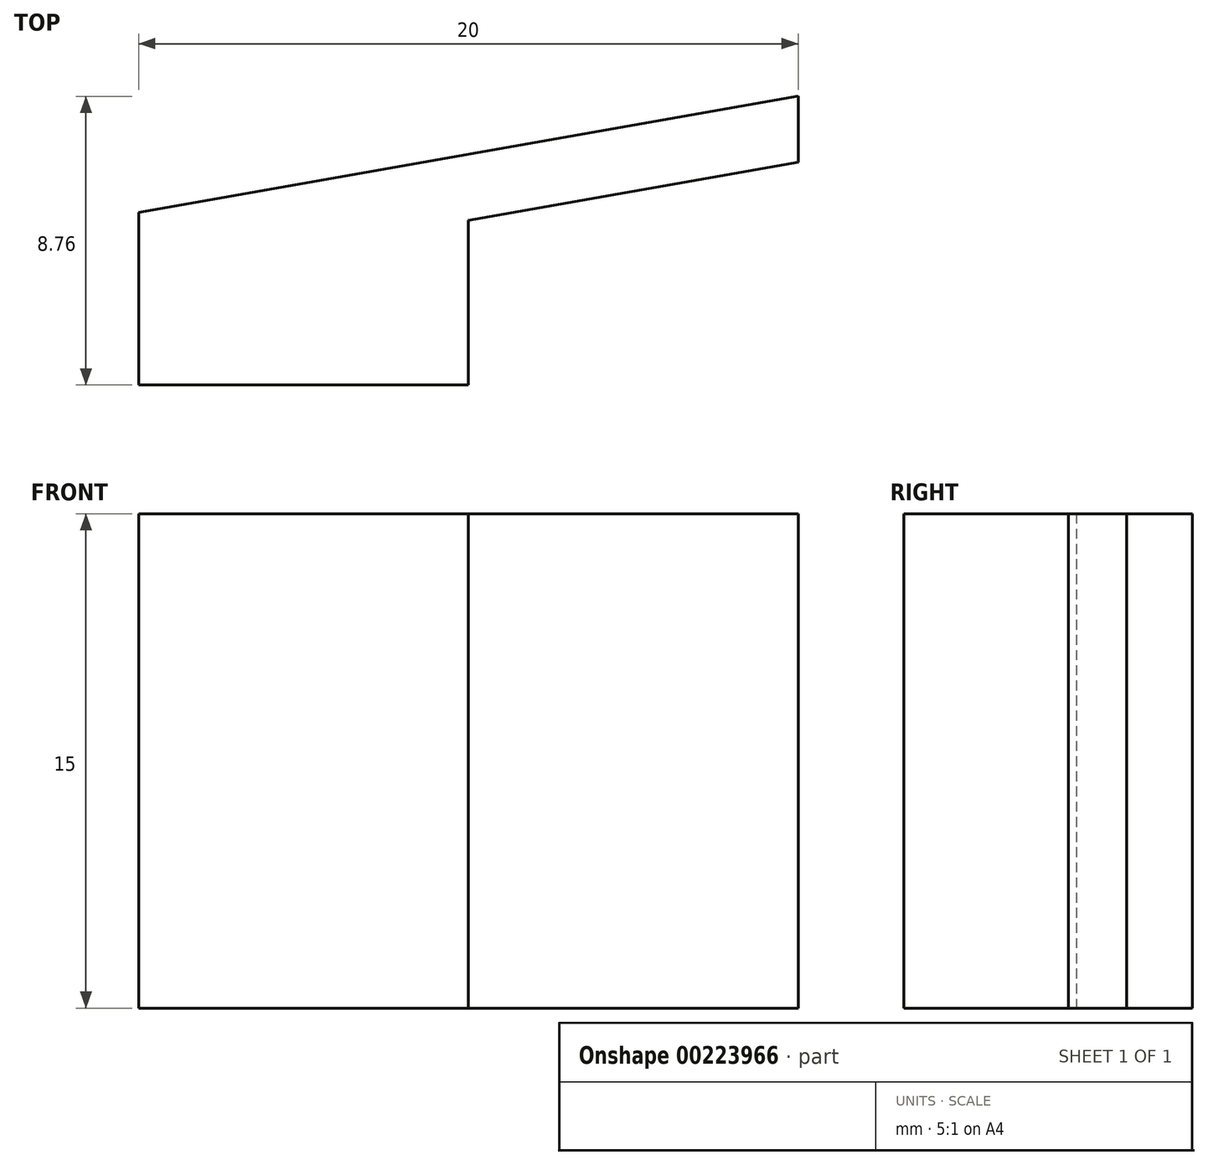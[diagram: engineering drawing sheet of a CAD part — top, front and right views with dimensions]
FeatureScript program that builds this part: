
annotation { "Feature Type Name" : "Feature", "Feature Type Description" : "" }
export const myFeature = defineFeature(function(context is Context, id is Id, definition is map)
    precondition{}
    {
        {
            var Q0;
            Q0=qCreatedBy(makeId("Top.planeOp"),FACE);
            var sketch = newSketch(context, id + "F0", { "sketchPlane" : qUnion([Q0])});
            skLineSegment(sketch, "E0", {"start": v(0, 0) * mm, "end": v(10, 0) * mm});
            skLineSegment(sketch, "E1", {"start": v(10, 0) * mm, "end": v(10, 5) * mm});
            skLineSegment(sketch, "E2", {"start": v(10, 5) * mm, "end": v(20, 6.76) * mm});
            skLineSegment(sketch, "E3", {"start": v(20, 6.76) * mm, "end": v(20, 8.76) * mm});
            skLineSegment(sketch, "E4", {"start": v(20, 8.76) * mm, "end": v(0, 5.24) * mm});
            skLineSegment(sketch, "E5", {"start": v(0, 5.24) * mm, "end": v(0, 0) * mm});
            skSolve(sketch);
        }
        {
            var Q0;
            Q0 = qSketchRegion(id + "F0", true);
            extrude(context, id + "F1", {"entities" : qUnion([Q0]), "depth" : 15 * mm});
        }
    });
